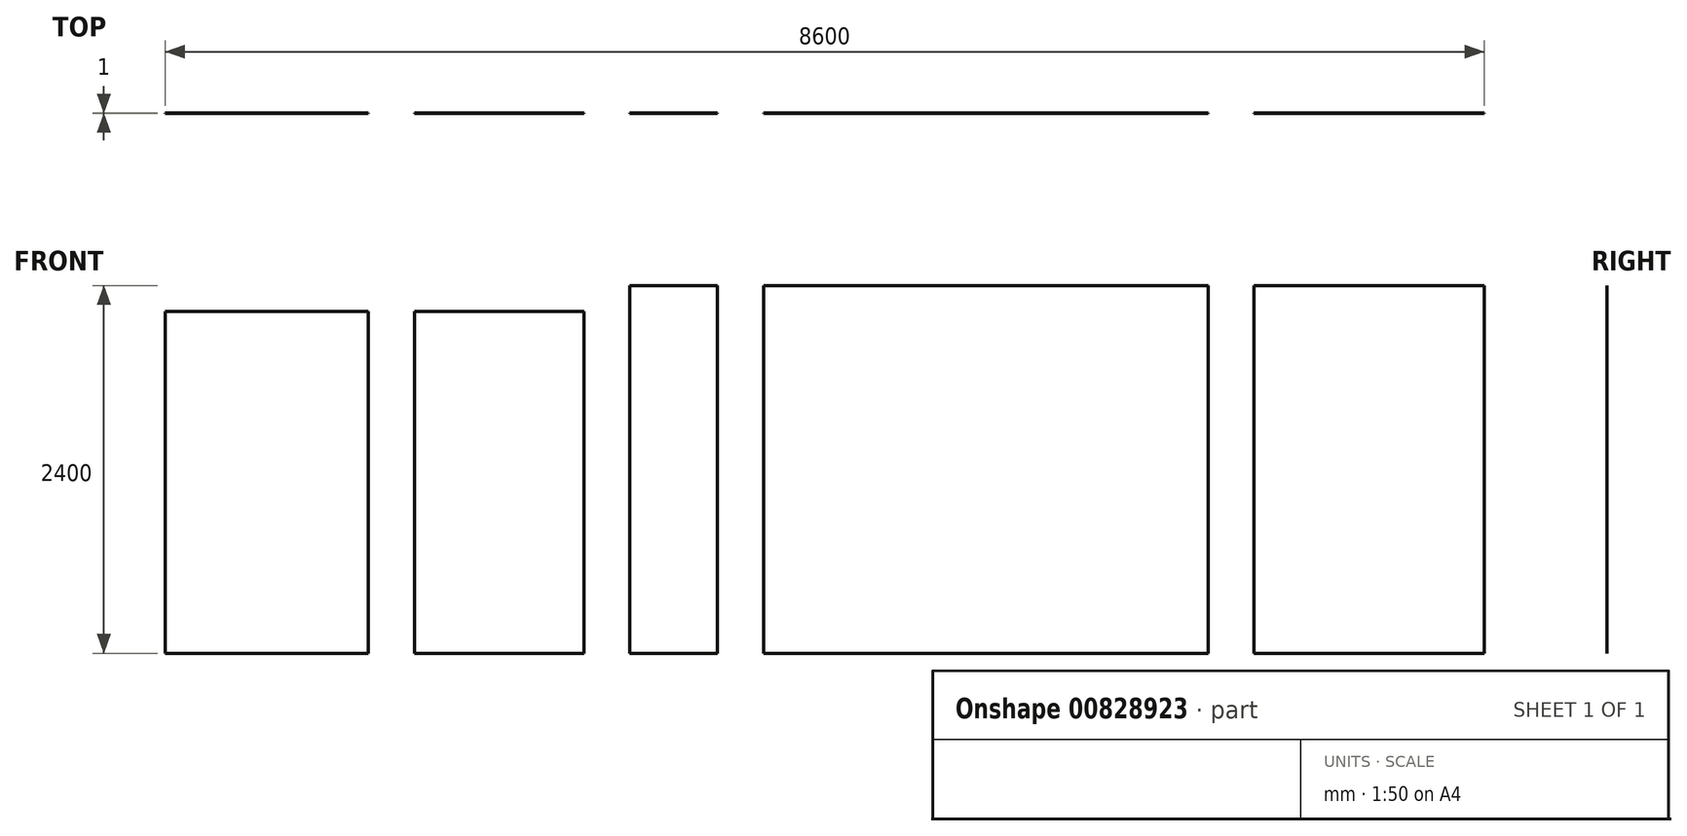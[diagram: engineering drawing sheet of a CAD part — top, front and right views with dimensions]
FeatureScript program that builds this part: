
annotation { "Feature Type Name" : "Feature", "Feature Type Description" : "" }
export const myFeature = defineFeature(function(context is Context, id is Id, definition is map)
    precondition{}
    {
        {
            var Q0;
            Q0=qCreatedBy(makeId("Front.planeOp"),FACE);
            var sketch = newSketch(context, id + "F0", { "sketchPlane" : qUnion([Q0])});
            skLineSegment(sketch, "E0.bottom", {"start": v(0, 0) * mm, "end": v(1325, 0) * mm});
            skLineSegment(sketch, "E0.top", {"start": v(0, 2230) * mm, "end": v(1325, 2230) * mm});
            skLineSegment(sketch, "E0.left", {"start": v(0, 0) * mm, "end": v(0, 2230) * mm});
            skLineSegment(sketch, "E0.right", {"start": v(1325, 0) * mm, "end": v(1325, 2230) * mm});
            skLineSegment(sketch, "E1", {"start": v(1625, 0) * mm, "end": v(1625, 2230) * mm});
            skLineSegment(sketch, "E2", {"start": v(1625, 2230) * mm, "end": v(2730, 2230) * mm});
            skLineSegment(sketch, "E3", {"start": v(2730, 2230) * mm, "end": v(2730, 0) * mm});
            skLineSegment(sketch, "E4", {"start": v(2730, 0) * mm, "end": v(1625, 0) * mm});
            skLineSegment(sketch, "E5", {"start": v(3030, 0) * mm, "end": v(3030, 2230) * mm});
            skLineSegment(sketch, "E6", {"start": v(3600, 2230) * mm, "end": v(3600, 0) * mm});
            skLineSegment(sketch, "E7", {"start": v(3600, 0) * mm, "end": v(3030, 0) * mm});
            skLineSegment(sketch, "E8", {"start": v(3900, 0) * mm, "end": v(3900, 2230) * mm});
            skLineSegment(sketch, "E9", {"start": v(6800, 2230) * mm, "end": v(6800, 0) * mm});
            skLineSegment(sketch, "E10", {"start": v(6800, 0) * mm, "end": v(3900, 0) * mm});
            skLineSegment(sketch, "E11", {"start": v(7100, 0) * mm, "end": v(7100, 2230) * mm});
            skLineSegment(sketch, "E12", {"start": v(8600, 2230) * mm, "end": v(8600, 0) * mm});
            skLineSegment(sketch, "E13", {"start": v(8600, 0) * mm, "end": v(7100, 0) * mm});
            skLineSegment(sketch, "E14", {"start": v(3900, 0) * mm, "end": v(3900, 2400) * mm});
            skLineSegment(sketch, "E15", {"start": v(3900, 2400) * mm, "end": v(6800, 2400) * mm});
            skLineSegment(sketch, "E16", {"start": v(6800, 2400) * mm, "end": v(6800, 2230) * mm});
            skLineSegment(sketch, "E17", {"start": v(7100, 2230) * mm, "end": v(7100, 2400) * mm});
            skLineSegment(sketch, "E18", {"start": v(7100, 2400) * mm, "end": v(8600, 2400) * mm});
            skLineSegment(sketch, "E19", {"start": v(8600, 2400) * mm, "end": v(8600, 2230) * mm});
            skLineSegment(sketch, "E20", {"start": v(3600, 2230) * mm, "end": v(3600, 2400) * mm});
            skLineSegment(sketch, "E21", {"start": v(3600, 2400) * mm, "end": v(3030, 2400) * mm});
            skLineSegment(sketch, "E22", {"start": v(3030, 2400) * mm, "end": v(3030, 2230) * mm});
            skSolve(sketch);
        }
        {
            var Q0;
            Q0=makeQuery(id+"F0.imprint","IMPRINT",FACE,{"disambiguationData":[TD([[makeQuery(id+"F0.imprint","IMPRINT",EDGE,{"derivedFrom":sQuery(id+"F0.wireOp",EDGE,"E0.bottom")}),1.0]])]});
            extrude(context, id + "F1", {"entities" : qUnion([Q0]), "depth" : 1 * mm, "offsetDistance" : 25 * mm});
        }
        {
            var Q0;
            Q0=qSketchRegion(id+"F0",true);
            extrude(context, id + "F2", {"entities" : qUnion([Q0]), "operationType" : NewBodyOperationType.ADD, "depth" : 1 * mm, "offsetDistance" : 25 * mm});
        }
    });
